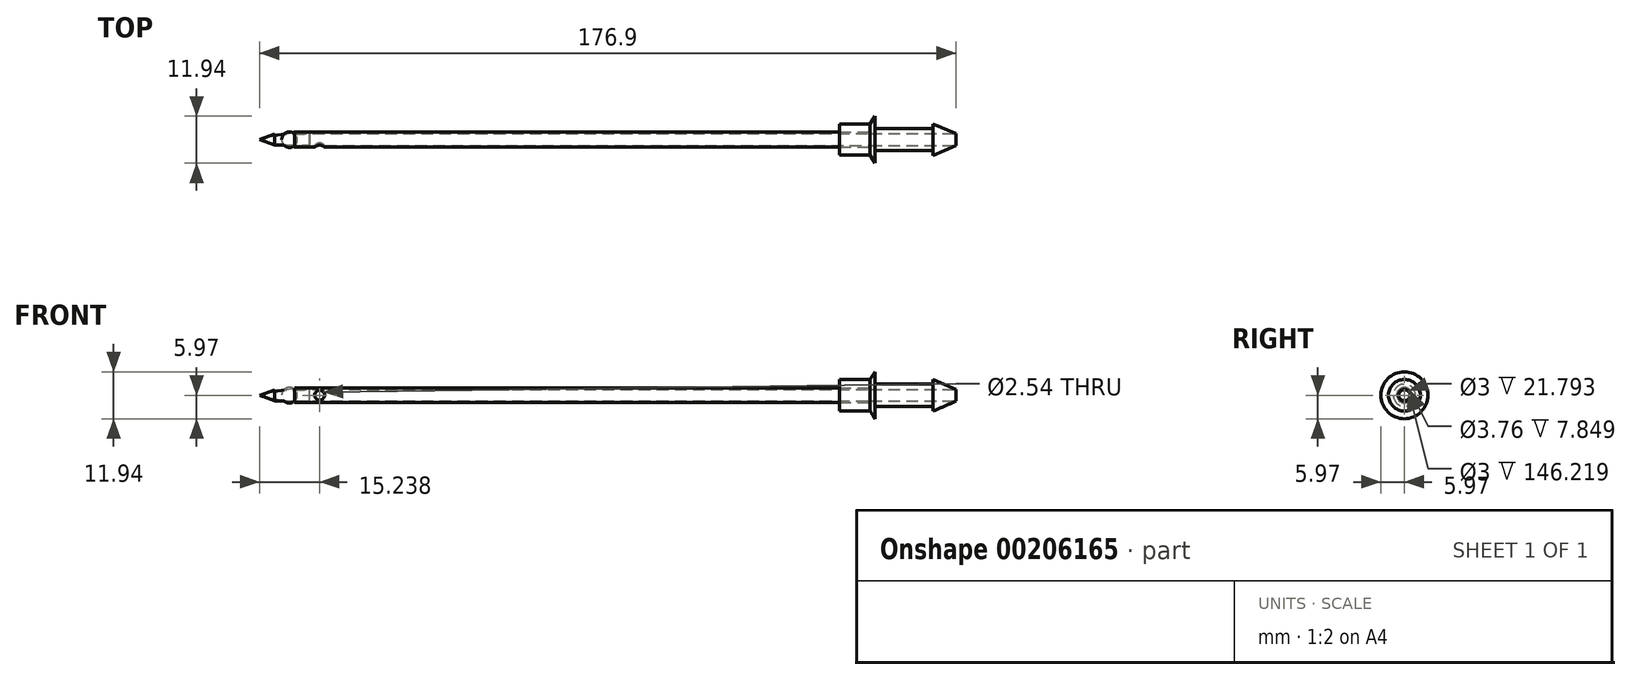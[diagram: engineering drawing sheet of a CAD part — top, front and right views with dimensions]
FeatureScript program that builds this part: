
annotation { "Feature Type Name" : "Feature", "Feature Type Description" : "" }
export const myFeature = defineFeature(function(context is Context, id is Id, definition is map)
    precondition{}
    {
        {
            var Q0;
            Q0=qCreatedBy(makeId("Front.planeOp"),FACE);
            var sketch = newSketch(context, id + "F0", { "sketchPlane" : qUnion([Q0])});
            skLineSegment(sketch, "E0", {"start": v(0, 0) * mm, "end": v(-182.04, 0) * mm, "construction": true});
            skLineSegment(sketch, "E1", {"start": v(-182.04, 1.5) * mm, "end": v(0, 1.5) * mm});
            skLineSegment(sketch, "E2", {"start": v(0, 1.5) * mm, "end": v(-5.9, 4.03) * mm});
            skLineSegment(sketch, "E3", {"start": v(-5.9, 4.03) * mm, "end": v(-5.9, 2.82) * mm});
            skLineSegment(sketch, "E4", {"start": v(-5.9, 2.82) * mm, "end": v(-20.62, 2.82) * mm});
            skLineSegment(sketch, "E5", {"start": v(-20.62, 2.82) * mm, "end": v(-20.62, 5.97) * mm});
            skLineSegment(sketch, "E6", {"start": v(-20.62, 5.97) * mm, "end": v(-21.8, 3.96) * mm});
            skLineSegment(sketch, "E7", {"start": v(-21.8, 3.96) * mm, "end": v(-29.64, 3.96) * mm});
            skLineSegment(sketch, "E8", {"start": v(-29.64, 3.96) * mm, "end": v(-29.64, 1.88) * mm});
            skLineSegment(sketch, "E9", {"start": v(-29.64, 1.88) * mm, "end": v(-182.04, 1.88) * mm});
            skLineSegment(sketch, "E10", {"start": v(-182.04, 1.88) * mm, "end": v(-182.04, 1.5) * mm});
            skLineSegment(sketch, "E11", {"start": v(-29.64, 1.88) * mm, "end": v(-21.8, 1.88) * mm});
            skLineSegment(sketch, "E12", {"start": v(-21.8, 1.88) * mm, "end": v(-21.8, 1.5) * mm});
            skSolve(sketch);
        }
        {
            var Q0;
            Q0=makeQuery(id+"F0.imprint","IMPRINT",FACE,{"disambiguationData":[TD([[makeQuery(id+"F0.imprint","IMPRINT",EDGE,{"derivedFrom":sQuery(id+"F0.wireOp",EDGE,"E9")}),1.0]])]});
            var Q1;
            Q1=sQuery(id+"F0.wireOp",EDGE,"E0");
            revolve(context, id + "F1", {"entities" : qUnion([Q0]), "axis" : qUnion([Q1]), "revolveType" : RevolveType.FULL});
        }
        {
            var Q0;
            {var subQ0=sQuery(id+"F0.wireOp",EDGE,"E2");Q0=makeQuery(id+"F0.imprint","IMPRINT",FACE,{"disambiguationData":[TD([[makeQuery(id+"F0.imprint","IMPRINT",EDGE,{"derivedFrom":subQ0}),1.0]])]});}
            var Q1;
            Q1=sQuery(id+"F0.wireOp",EDGE,"E0");
            revolve(context, id + "F2", {"entities" : qUnion([Q0]), "axis" : qUnion([Q1]), "revolveType" : RevolveType.FULL});
        }
        {
            var Q0;
            Q0=qCreatedBy(makeId("Front.planeOp"),FACE);
            var sketch = newSketch(context, id + "F3", { "sketchPlane" : qUnion([Q0])});
            skLineSegment(sketch, "E13", {"start": v(-182.04, 1.88) * mm, "end": v(-182.04, -1.88) * mm});
            skLineSegment(sketch, "E14", {"start": v(-182.04, -1.88) * mm, "end": v(-168.01, 1.88) * mm, "construction": true});
            skLineSegment(sketch, "E15", {"start": v(-168.01, 1.88) * mm, "end": v(-182.04, 1.88) * mm});
            skLineSegment(sketch, "E16", {"start": v(-29.64, -1.88) * mm, "end": v(-182.04, -1.88) * mm, "construction": true});
            skLineSegment(sketch, "E17", {"start": v(-182.04, 1.88) * mm, "end": v(-29.64, 1.88) * mm, "construction": true});
            skLineSegment(sketch, "E18", {"start": v(-168.01, 1.88) * mm, "end": v(-168.01, -1.88) * mm});
            skLineSegment(sketch, "E19", {"start": v(-168.01, -1.88) * mm, "end": v(-182.04, -1.88) * mm});
            skSolve(sketch);
        }
        {
            var Q0;
            Q0 = qSketchRegion(id + "F3", true);
            extrude(context, id + "F4", {"entities" : qUnion([Q0]), "operationType" : NewBodyOperationType.REMOVE, "endBound" : BoundingType.THROUGH_ALL, "oppositeDirection" : true, "depth" : 25.4 * mm, "hasSecondDirection" : true, "secondDirectionBound" : SecondDirectionBoundingType.THROUGH_ALL, "secondDirectionOppositeDirection" : false, "secondDirectionDepth" : 25.4 * mm});
        }
        {
            var Q0;
            Q0=qCreatedBy(makeId("Front.planeOp"),FACE);
            var sketch = newSketch(context, id + "F5", { "sketchPlane" : qUnion([Q0])});
            skLineSegment(sketch, "E20.0", {"start": v(-168.01, 1.88) * mm, "end": v(-168.01, 0) * mm});
            skLineSegment(sketch, "E21", {"start": v(-168.01, 0) * mm, "end": v(-175.63, 0) * mm});
            skPoint(sketch, "E22.orphan", {"position": v(-168.01, -1.88) * mm});
            skLineSegment(sketch, "E23", {"start": v(-168.01, 0) * mm, "end": v(-179.12, 0) * mm, "construction": true});
            skLineSegment(sketch, "E24", {"start": v(-168.01, 1.88) * mm, "end": v(-175.1, 0.63) * mm});
            skArc(sketch, "E25", {"start": v(-175.1, 0.63) * mm, "mid": v(-175.48, 0.41) * mm, "end": v(-175.63, 0) * mm});
            skLineSegment(sketch, "E26", {"start": v(-168.01, 1.88) * mm, "end": v(-166.1, 1.88) * mm, "construction": true});
            skSolve(sketch);
        }
        {
            var Q0;
            Q0 = qSketchRegion(id + "F5", true);
            var Q1;
            Q1=sQuery(id+"F5.wireOp",EDGE,"E23");
            revolve(context, id + "F6", {"operationType" : NewBodyOperationType.ADD, "entities" : qUnion([Q0]), "axis" : qUnion([Q1]), "revolveType" : RevolveType.FULL});
        }
        {
            var Q0;
            Q0=qCreatedBy(makeId("Front.planeOp"),FACE);
            var sketch = newSketch(context, id + "F7", { "sketchPlane" : qUnion([Q0])});
            skLineSegment(sketch, "E27", {"start": v(0, -1.5) * mm, "end": v(-168.01, -1.5) * mm, "construction": true});
            skLineSegment(sketch, "E28", {"start": v(-168.01, 1.5) * mm, "end": v(0, 1.5) * mm, "construction": true});
            skLineSegment(sketch, "E29", {"start": v(-161.66, 1.5) * mm, "end": v(-161.66, -1.5) * mm, "construction": true});
            skCircle(sketch, "E30", {"center": v(-161.66, 0) * mm, "radius": 1.27 * mm});
            skSolve(sketch);
        }
        {
            var Q0;
            Q0 = qSketchRegion(id + "F7", true);
            extrude(context, id + "F8", {"entities" : qUnion([Q0]), "operationType" : NewBodyOperationType.REMOVE, "endBound" : BoundingType.THROUGH_ALL, "depth" : 25.4 * mm});
        }
        {
            var Q0;
            Q0=qCreatedBy(makeId("Front.planeOp"),FACE);
            var sketch = newSketch(context, id + "F9", { "sketchPlane" : qUnion([Q0])});
            skArc(sketch, "E31", {"start": v(-169.31, -1.98) * mm, "mid": v(-167.33, 0) * mm, "end": v(-169.31, 1.98) * mm});
            skLineSegment(sketch, "E32", {"start": v(-169.31, -1.98) * mm, "end": v(-169.31, 1.98) * mm});
            skLineSegment(sketch, "E33", {"start": v(0, -1.5) * mm, "end": v(-168.01, -1.5) * mm, "construction": true});
            skLineSegment(sketch, "E34", {"start": v(-168.01, 1.5) * mm, "end": v(0, 1.5) * mm, "construction": true});
            skLineSegment(sketch, "E35", {"start": v(-169.31, 0) * mm, "end": v(-169.31, 2.65) * mm, "construction": true});
            skSolve(sketch);
        }
        {
            var Q0;
            Q0 = qSketchRegion(id + "F9", true);
            var Q1;
            Q1=sQuery(id+"F9.wireOp",EDGE,"E35");
            revolve(context, id + "F10", {"entities" : qUnion([Q0]), "axis" : qUnion([Q1]), "revolveType" : RevolveType.FULL});
        }
        {
            var Q0;
            Q0=qCreatedBy(makeId("Front.planeOp"),FACE);
            var sketch = newSketch(context, id + "F11", { "sketchPlane" : qUnion([Q0])});
            skLineSegment(sketch, "E36.0", {"start": v(-168.01, 1.88) * mm, "end": v(-168.01, -1.88) * mm, "construction": true});
            skLineSegment(sketch, "E37", {"start": v(-168.01, 0) * mm, "end": v(-180.12, 0) * mm, "construction": true});
            skPoint(sketch, "E37.endSnap0", {"position": v(-168.01, 0) * mm});
            skLineSegment(sketch, "E38", {"start": v(-173.06, 1.4) * mm, "end": v(-164.2, 1.4) * mm});
            skLineSegment(sketch, "E39", {"start": v(-164.2, 1.4) * mm, "end": v(-164.2, 0) * mm});
            skLineSegment(sketch, "E40", {"start": v(-164.2, 0) * mm, "end": v(-176.9, 0) * mm});
            skLineSegment(sketch, "E41", {"start": v(-173.06, 1.4) * mm, "end": v(-176.9, 0) * mm});
            skSolve(sketch);
        }
        {
            var Q0;
            Q0=makeQuery(id+"F11.imprint","IMPRINT",FACE,{"disambiguationData":[TD([[makeQuery(id+"F11.imprint","IMPRINT",EDGE,{"derivedFrom":sQuery(id+"F11.wireOp",EDGE,"E38")}),-1.0]])]});
            var Q1;
            Q1=sQuery(id+"F11.wireOp",EDGE,"E37");
            revolve(context, id + "F12", {"entities" : qUnion([Q0]), "axis" : qUnion([Q1]), "revolveType" : RevolveType.FULL});
        }
    });
